# Revit family: Midmark - 56 - Wall Mount Digital Dental Radiography System
name_source: partatom
category: Specialty Equipment
revit_build: Autodesk Revit 2017 (Build: 20190508_0315(x64)
units: mm (PartAtom-declared; Revit-internal decimal feet)

## family parameters
Always vertical = Yes
Cut with Voids When Loaded = No
Part Type = Normal
Room Calculation Point = No
Round Connector Dimension = Use Diameter
Shared = No
Work Plane-Based = No

## types (2) — shared parameters
Closed Arm = Yes
Description = Coordinate cable needs upon ordering
Extended Arm = No
Joint Connections = Midmark - Warm Gray
Manufacturer = Midmark
Mount Plate = Midmark - White
Wall Mount = Midmark - White
X-Ray Arm = Midmark - White
X-Ray Extension = Midmark - White
X-Ray Head = Midmark - White
X-Ray Wall Mount = Midmark - White

## per-type parameters (varying)
| type | Model | Type Comments |
| Wall Mount Assembly - 56" - #1 Digital Sensor | DCV5-G2A/H/S3 | Midmark Complete, 56" 2 Stud, Handswitch, #1 Digital Sensor |
| Wall Mount Assembly - 56" - #2 Digital Sensor | DCV5-G2A/H/S4 | Midmark Complete, 56" 2 Stud, Handswitch, #2 Digital Sensor |

## geometry (parser evidence)
native form markers: Sweep x3
no freeform markers — native parametric forms only
